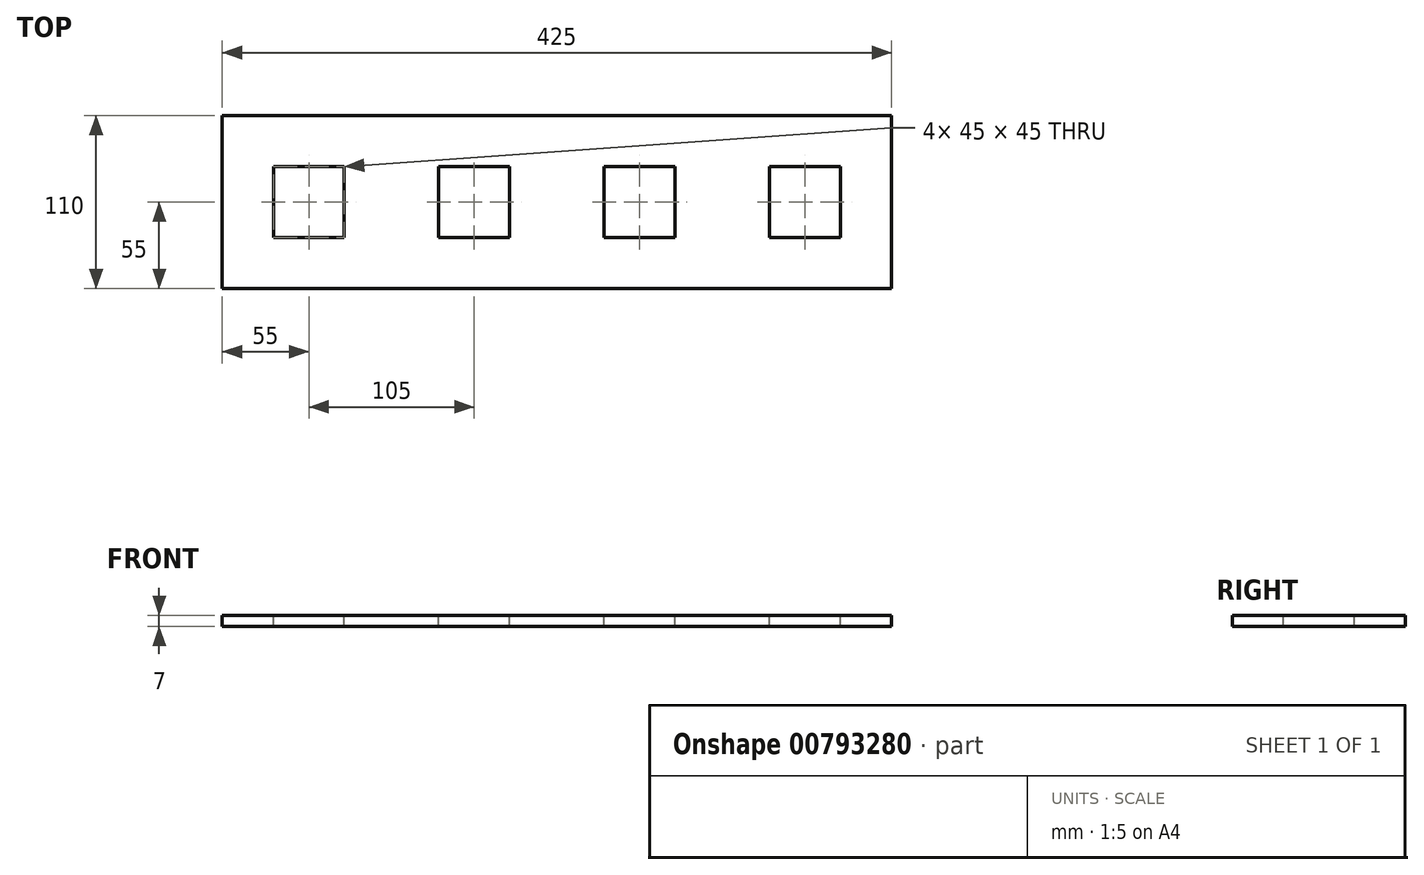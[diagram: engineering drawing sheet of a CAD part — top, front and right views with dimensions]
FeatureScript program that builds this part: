
annotation { "Feature Type Name" : "Feature", "Feature Type Description" : "" }
export const myFeature = defineFeature(function(context is Context, id is Id, definition is map)
    precondition{}
    {
        {
            var Q0;
            Q0=qCreatedBy(makeId("Top.planeOp"),FACE);
            var sketch = newSketch(context, id + "F0", { "sketchPlane" : qUnion([Q0])});
            skLineSegment(sketch, "E0.bottom", {"start": v(205, -55) * mm, "end": v(-205, -55) * mm});
            skLineSegment(sketch, "E0.top", {"start": v(205, 55) * mm, "end": v(-205, 55) * mm});
            skLineSegment(sketch, "E0.left", {"start": v(205, -55) * mm, "end": v(205, 55) * mm});
            skLineSegment(sketch, "E0.right", {"start": v(-205, -55) * mm, "end": v(-205, 55) * mm});
            skPoint(sketch, "E0.middle", {"position": v(0, 0) * mm});
            skLineSegment(sketch, "E1.bottom", {"start": v(-205, -55) * mm, "end": v(-220, -55) * mm});
            skLineSegment(sketch, "E1.top", {"start": v(-205, 55) * mm, "end": v(-220, 55) * mm});
            skLineSegment(sketch, "E1.right", {"start": v(-220, -55) * mm, "end": v(-220, 55) * mm});
            skSolve(sketch);
        }
        {
            var Q0;
            Q0=makeQuery(id+"F0.imprint","IMPRINT",FACE,{"disambiguationData":[TD([[makeQuery(id+"F0.imprint","IMPRINT",EDGE,{"derivedFrom":sQuery(id+"F0.wireOp",EDGE,"E0.bottom")}),-1.0]])]});
            extrude(context, id + "F1", {"entities" : qUnion([Q0]), "depth" : 7 * mm, "offsetDistance" : 25 * mm});
        }
        {
            var Q0;
            Q0=makeQuery(id+"F1.opExtrude","CAP_FACE",FACE,{"disambiguationData":[OSD([sQuery(id+"F0.wireOp",EDGE,"E0.bottom"),sQuery(id+"F0.wireOp",EDGE,"E0.top"),sQuery(id+"F0.wireOp",EDGE,"E0.left"),sQuery(id+"F0.wireOp",EDGE,"E0.right")])],"isStart":false});
            var sketch = newSketch(context, id + "F2", { "sketchPlane" : qUnion([Q0])});
            skLineSegment(sketch, "E2.bottom", {"start": v(172.5, 22.5) * mm, "end": v(127.5, 22.5) * mm});
            skLineSegment(sketch, "E2.top", {"start": v(172.5, -22.5) * mm, "end": v(127.5, -22.5) * mm});
            skLineSegment(sketch, "E2.left", {"start": v(172.5, 22.5) * mm, "end": v(172.5, -22.5) * mm});
            skLineSegment(sketch, "E2.right", {"start": v(127.5, 22.5) * mm, "end": v(127.5, -22.5) * mm});
            skPoint(sketch, "E2.middle", {"position": v(150, 0) * mm});
            skLineSegment(sketch, "E3.bottom", {"start": v(67.5, -22.5) * mm, "end": v(22.5, -22.5) * mm});
            skLineSegment(sketch, "E3.top", {"start": v(67.5, 22.5) * mm, "end": v(22.5, 22.5) * mm});
            skLineSegment(sketch, "E3.left", {"start": v(67.5, -22.5) * mm, "end": v(67.5, 22.5) * mm});
            skLineSegment(sketch, "E3.right", {"start": v(22.5, -22.5) * mm, "end": v(22.5, 22.5) * mm});
            skPoint(sketch, "E3.middle", {"position": v(45, 0) * mm});
            skLineSegment(sketch, "E4.bottom", {"start": v(-37.5, -22.5) * mm, "end": v(-82.5, -22.5) * mm});
            skLineSegment(sketch, "E4.top", {"start": v(-37.5, 22.5) * mm, "end": v(-82.5, 22.5) * mm});
            skLineSegment(sketch, "E4.left", {"start": v(-37.5, -22.5) * mm, "end": v(-37.5, 22.5) * mm});
            skLineSegment(sketch, "E4.right", {"start": v(-82.5, -22.5) * mm, "end": v(-82.5, 22.5) * mm});
            skPoint(sketch, "E4.middle", {"position": v(-60, 0) * mm});
            skPoint(sketch, "E5.middle", {"position": v(0, 0) * mm});
            skLineSegment(sketch, "E6.bottom", {"start": v(-142.5, -22.5) * mm, "end": v(-187.5, -22.5) * mm});
            skLineSegment(sketch, "E6.top", {"start": v(-142.5, 22.5) * mm, "end": v(-187.5, 22.5) * mm});
            skLineSegment(sketch, "E6.left", {"start": v(-142.5, -22.5) * mm, "end": v(-142.5, 22.5) * mm});
            skLineSegment(sketch, "E6.right", {"start": v(-187.5, -22.5) * mm, "end": v(-187.5, 22.5) * mm});
            skPoint(sketch, "E6.middle", {"position": v(-165, 0) * mm});
            skSolve(sketch);
        }
        {
            var Q0;
            Q0=makeQuery(id+"F2.imprint","IMPRINT",FACE,{"disambiguationData":[TD([[makeQuery(id+"F2.imprint","IMPRINT",EDGE,{"derivedFrom":sQuery(id+"F2.wireOp",EDGE,"E4.bottom")}),-1.0]])]});
            var Q1;
            Q1=makeQuery(id+"F2.imprint","IMPRINT",FACE,{"disambiguationData":[TD([[makeQuery(id+"F2.imprint","IMPRINT",EDGE,{"derivedFrom":sQuery(id+"F2.wireOp",EDGE,"E5.bottom")}),-1.0]])]});
            var Q2;
            Q2=makeQuery(id+"F2.imprint","IMPRINT",FACE,{"disambiguationData":[TD([[makeQuery(id+"F2.imprint","IMPRINT",EDGE,{"derivedFrom":sQuery(id+"F2.wireOp",EDGE,"E3.bottom")}),-1.0]])]});
            var Q3;
            Q3=makeQuery(id+"F2.imprint","IMPRINT",FACE,{"disambiguationData":[TD([[makeQuery(id+"F2.imprint","IMPRINT",EDGE,{"derivedFrom":sQuery(id+"F2.wireOp",EDGE,"E2.bottom")}),1.0]])]});
            var Q4;
            Q4=makeQuery(id+"F2.imprint","IMPRINT",FACE,{"disambiguationData":[TD([[makeQuery(id+"F2.imprint","IMPRINT",EDGE,{"derivedFrom":sQuery(id+"F2.wireOp",EDGE,"E6.bottom")}),-1.0]])]});
            extrude(context, id + "F3", {"entities" : qUnion([Q0, Q1, Q2, Q3, Q4]), "operationType" : NewBodyOperationType.REMOVE, "oppositeDirection" : true, "depth" : 25 * mm, "offsetDistance" : 25 * mm});
        }
        {
            var Q0;
            Q0=makeQuery(id+"F0.imprint","IMPRINT",FACE,{"disambiguationData":[TD([[makeQuery(id+"F0.imprint","IMPRINT",EDGE,{"derivedFrom":sQuery(id+"F0.wireOp",EDGE,"E1.bottom")}),-1.0]])]});
            extrude(context, id + "F4", {"entities" : qUnion([Q0]), "operationType" : NewBodyOperationType.ADD, "depth" : 7 * mm, "offsetDistance" : 25 * mm});
        }
    });
